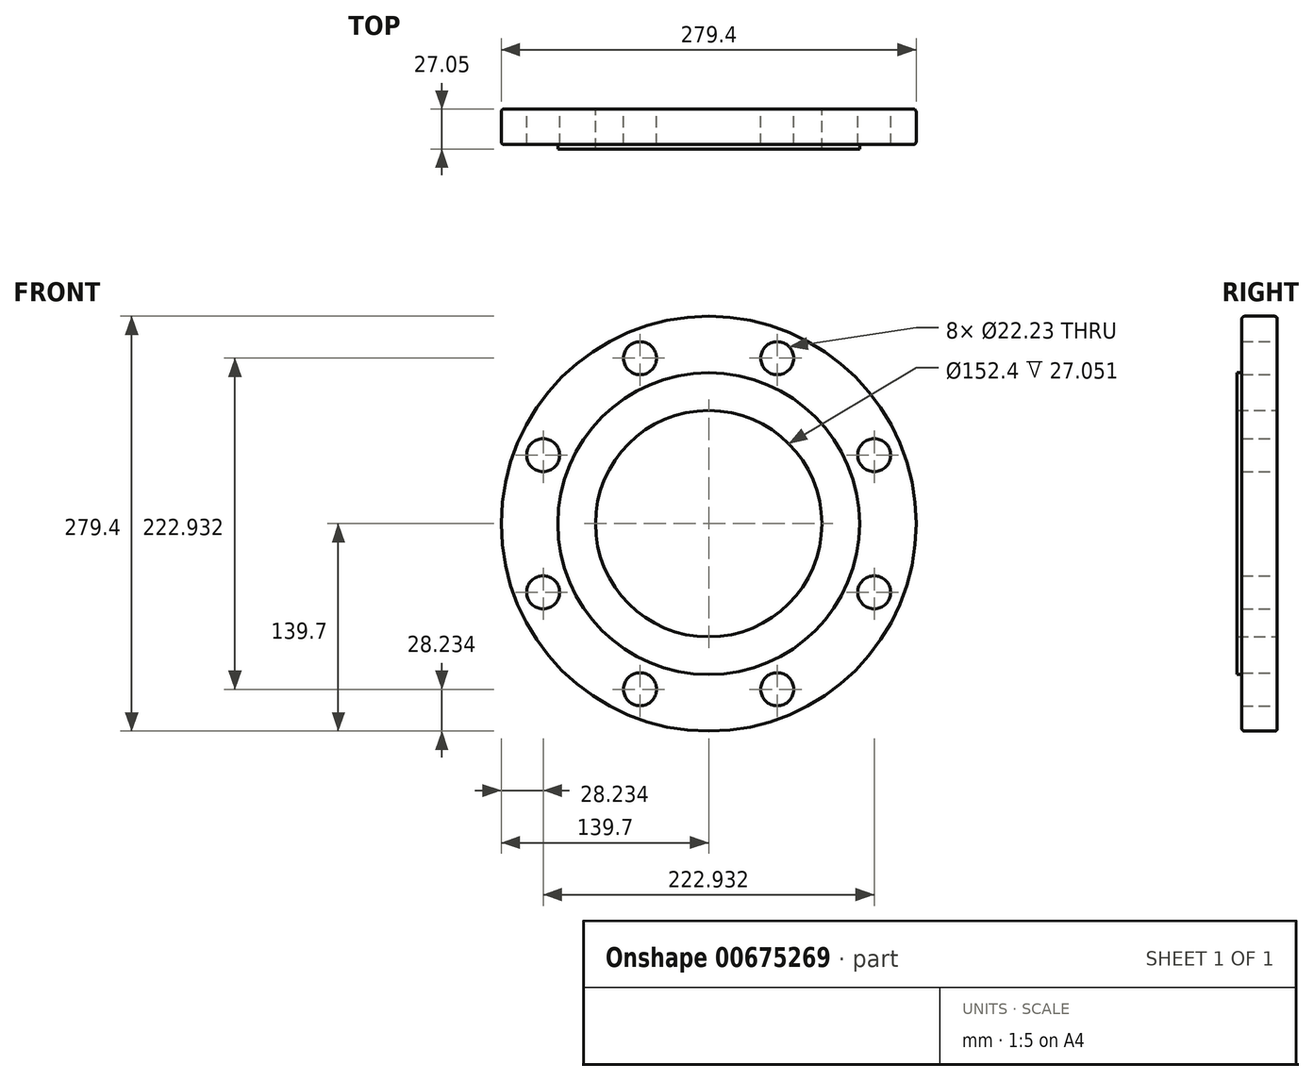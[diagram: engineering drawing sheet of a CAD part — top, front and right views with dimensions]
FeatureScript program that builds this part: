
annotation { "Feature Type Name" : "Feature", "Feature Type Description" : "" }
export const myFeature = defineFeature(function(context is Context, id is Id, definition is map)
    precondition{}
    {
        {
            var Q0;
            Q0=qCreatedBy(makeId("Front.planeOp"),FACE);
            var sketch = newSketch(context, id + "F0", { "sketchPlane" : qUnion([Q0])});
            skCircle(sketch, "E0", {"center": v(0, 0) * mm, "radius": 76.2 * mm});
            skCircle(sketch, "E1", {"center": v(0, 0) * mm, "radius": 139.7 * mm});
            skCircle(sketch, "E2", {"center": v(0, 0) * mm, "radius": 120.65 * mm, "construction": true});
            skLineSegment(sketch, "E3", {"start": v(0, 0) * mm, "end": v(0, 167.15) * mm, "construction": true});
            skLineSegment(sketch, "E4", {"start": v(0, 0) * mm, "end": v(62.99, 152.07) * mm, "construction": true});
            skCircle(sketch, "E5", {"center": v(46.17, 111.47) * mm, "radius": 11.11 * mm});
            skCircle(sketch, "E6.1.0", {"center": v(-46.17, 111.47) * mm, "radius": 11.11 * mm});
            skCircle(sketch, "E6.2.0", {"center": v(-111.47, 46.17) * mm, "radius": 11.11 * mm});
            skCircle(sketch, "E6.3.0", {"center": v(-111.47, -46.17) * mm, "radius": 11.11 * mm});
            skCircle(sketch, "E6.4.0", {"center": v(-46.17, -111.47) * mm, "radius": 11.11 * mm});
            skCircle(sketch, "E6.5.0", {"center": v(46.17, -111.47) * mm, "radius": 11.11 * mm});
            skCircle(sketch, "E6.6.0", {"center": v(111.47, -46.17) * mm, "radius": 11.11 * mm});
            skCircle(sketch, "E6.7.0", {"center": v(111.47, 46.17) * mm, "radius": 11.11 * mm});
            skSolve(sketch);
        }
        {
            var Q0;
            Q0 = qSketchRegion(id + "F0", true);
            extrude(context, id + "F1", {"entities" : qUnion([Q0]), "depth" : 23.88 * mm, "offsetDistance" : 25.4 * mm});
        }
        {
            var Q0;
            Q0=makeQuery(id+"F1.opExtrude","CAP_FACE",FACE,{"disambiguationData":[OSD([sQuery(id+"F0.wireOp",EDGE,"E0"),sQuery(id+"F0.wireOp",EDGE,"E1"),sQuery(id+"F0.wireOp",EDGE,"E5"),sQuery(id+"F0.wireOp",EDGE,"E6.1.0"),sQuery(id+"F0.wireOp",EDGE,"E6.2.0"),sQuery(id+"F0.wireOp",EDGE,"E6.3.0"),sQuery(id+"F0.wireOp",EDGE,"E6.4.0"),sQuery(id+"F0.wireOp",EDGE,"E6.5.0"),sQuery(id+"F0.wireOp",EDGE,"E6.6.0"),sQuery(id+"F0.wireOp",EDGE,"E6.7.0")])],"isStart":false});
            var sketch = newSketch(context, id + "F2", { "sketchPlane" : qUnion([Q0])});
            skCircle(sketch, "E7", {"center": v(0, 0) * mm, "radius": 101.6 * mm});
            skCircle(sketch, "E8", {"center": v(0, 0) * mm, "radius": 76.2 * mm});
            skSolve(sketch);
        }
        {
            var Q0;
            Q0 = qSketchRegion(id + "F2", true);
            extrude(context, id + "F3", {"entities" : qUnion([Q0]), "operationType" : NewBodyOperationType.ADD, "depth" : 3.17 * mm, "offsetDistance" : 25.4 * mm});
        }
        {
            var Q0;
            Q0=makeQuery(id+"F1.opExtrude","CAP_EDGE",EDGE,{"disambiguationData":[OSD([sQuery(id+"F0.wireOp",EDGE,"E1")])],"isStart":true});
            var Q1;
            Q1=makeQuery(id+"F1.opExtrude","CAP_EDGE",EDGE,{"disambiguationData":[OSD([sQuery(id+"F0.wireOp",EDGE,"E1")])],"isStart":false});
            var Q2;
            Q2=makeQuery(id+"F3.opExtrude","CAP_EDGE",EDGE,{"disambiguationData":[OSD([sQuery(id+"F2.wireOp",EDGE,"E7")])],"isStart":true});
            fillet(context, id + "F4", {"entities" : qUnion([Q0, Q1, Q2]), "radius" : 1.9 * mm, "tangentPropagation" : true, "allowEdgeOverflow" : false});
        }
    });
